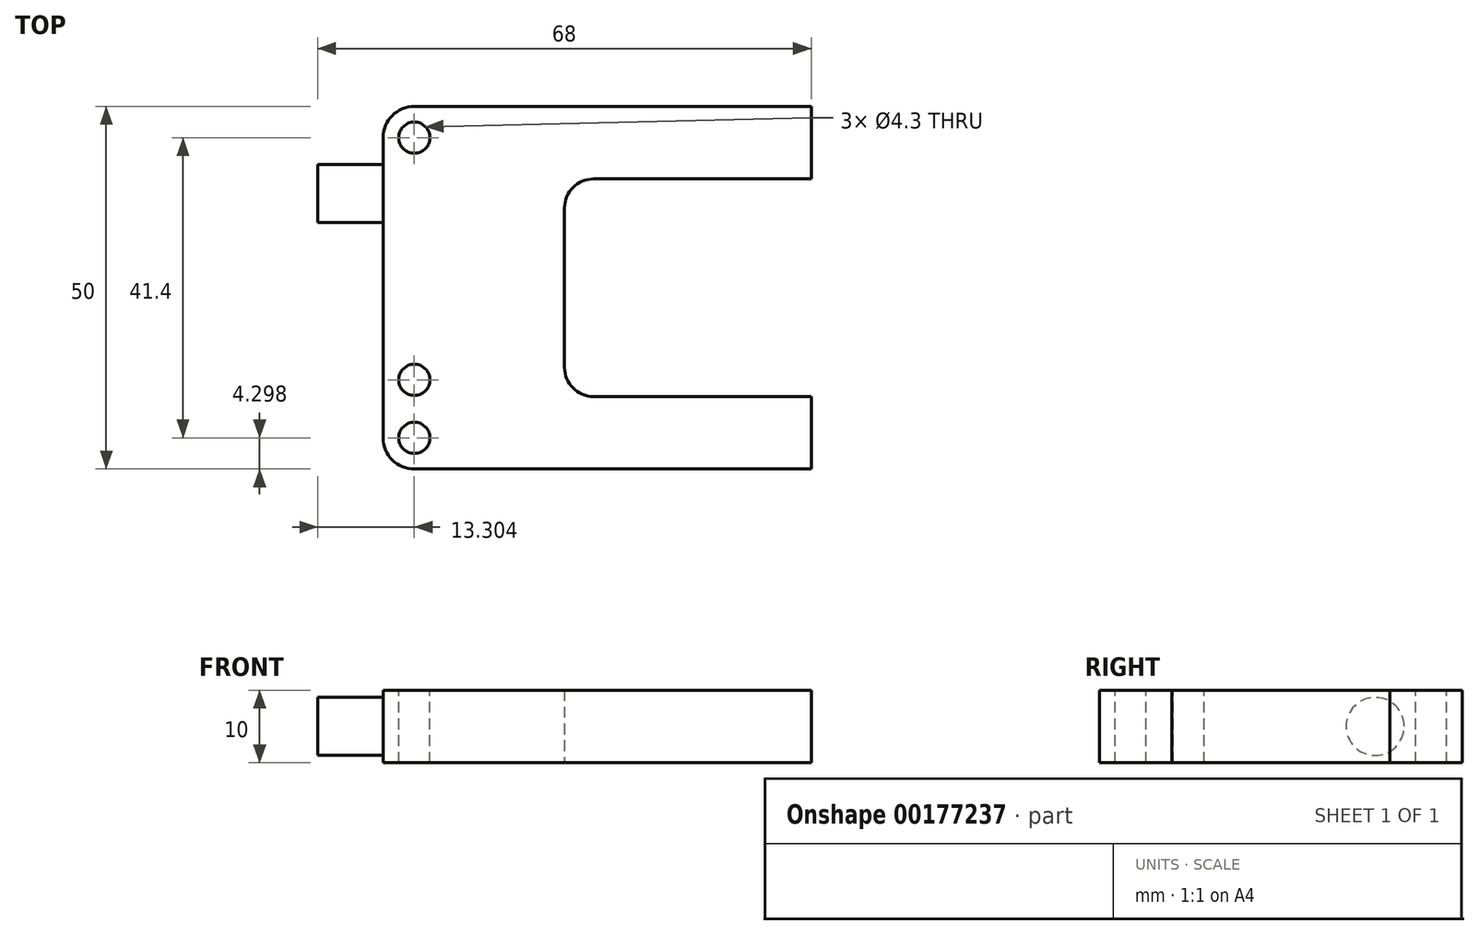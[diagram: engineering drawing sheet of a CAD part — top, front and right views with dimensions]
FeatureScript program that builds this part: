
annotation { "Feature Type Name" : "Feature", "Feature Type Description" : "" }
export const myFeature = defineFeature(function(context is Context, id is Id, definition is map)
    precondition{}
    {
        {
            var Q0;
            Q0=qCreatedBy(makeId("Top.planeOp"),FACE);
            var sketch = newSketch(context, id + "F0", { "sketchPlane" : qUnion([Q0])});
            skLineSegment(sketch, "E0", {"start": v(-16.13, 24.59) * mm, "end": v(42.87, 24.59) * mm});
            skLineSegment(sketch, "E1", {"start": v(42.87, 24.59) * mm, "end": v(42.87, 14.59) * mm});
            skLineSegment(sketch, "E2", {"start": v(42.87, 14.59) * mm, "end": v(8.87, 14.59) * mm});
            skLineSegment(sketch, "E3", {"start": v(8.87, 14.59) * mm, "end": v(8.87, -15.41) * mm});
            skLineSegment(sketch, "E4", {"start": v(8.87, -15.41) * mm, "end": v(42.87, -15.41) * mm});
            skLineSegment(sketch, "E5", {"start": v(42.87, -15.41) * mm, "end": v(42.87, -25.41) * mm});
            skLineSegment(sketch, "E6", {"start": v(42.87, -25.41) * mm, "end": v(-16.13, -25.41) * mm});
            skLineSegment(sketch, "E7", {"start": v(-16.13, -25.41) * mm, "end": v(-16.13, 24.59) * mm});
            skSolve(sketch);
        }
        {
            var Q0;
            Q0 = qSketchRegion(id + "F0", true);
            extrude(context, id + "F1", {"entities" : qUnion([Q0]), "depth" : 10 * mm});
        }
        {
            var Q0;
            Q0=makeQuery(id+"F1.opExtrude","SWEPT_EDGE",EDGE,{"disambiguationData":[OSD([sQuery(id+"F0.wireOp",EDGE,"E2"),sQuery(id+"F0.wireOp",EDGE,"E3")])]});
            var Q1;
            Q1=makeQuery(id+"F1.opExtrude","SWEPT_EDGE",EDGE,{"disambiguationData":[OSD([sQuery(id+"F0.wireOp",EDGE,"E3"),sQuery(id+"F0.wireOp",EDGE,"E4")])]});
            fillet(context, id + "F2", {"entities" : qUnion([Q0, Q1]), "radius" : 4 * mm, "tangentPropagation" : true, "allowEdgeOverflow" : false});
        }
        {
            var Q0;
            Q0=makeQuery(id+"F1.opExtrude","SWEPT_EDGE",EDGE,{"disambiguationData":[OSD([sQuery(id+"F0.wireOp",EDGE,"E0"),sQuery(id+"F0.wireOp",EDGE,"E7")])]});
            var Q1;
            Q1=makeQuery(id+"F1.opExtrude","SWEPT_EDGE",EDGE,{"disambiguationData":[OSD([sQuery(id+"F0.wireOp",EDGE,"E6"),sQuery(id+"F0.wireOp",EDGE,"E7")])]});
            fillet(context, id + "F3", {"entities" : qUnion([Q0, Q1]), "radius" : 4.3 * mm, "tangentPropagation" : true, "allowEdgeOverflow" : false});
        }
        {
            var Q0;
            Q0=makeQuery(id+"F1.opExtrude","CAP_FACE",FACE,{"disambiguationData":[OSD([sQuery(id+"F0.wireOp",EDGE,"E0"),sQuery(id+"F0.wireOp",EDGE,"E1"),sQuery(id+"F0.wireOp",EDGE,"E2"),sQuery(id+"F0.wireOp",EDGE,"E3"),sQuery(id+"F0.wireOp",EDGE,"E4"),sQuery(id+"F0.wireOp",EDGE,"E5"),sQuery(id+"F0.wireOp",EDGE,"E6"),sQuery(id+"F0.wireOp",EDGE,"E7")])],"isStart":false});
            var sketch = newSketch(context, id + "F4", { "sketchPlane" : qUnion([Q0])});
            skPoint(sketch, "E8", {"position": v(-11.83, 20.29) * mm});
            skPoint(sketch, "E9", {"position": v(-11.83, -21.11) * mm});
            skPoint(sketch, "E10", {"position": v(-11.83, -13.11) * mm});
            skSolve(sketch);
        }
        {
            var Q0;
            Q0=sQuery(id+"F4.wireOp",VERTEX,"E8");
            var Q1;
            Q1=sQuery(id+"F4.wireOp",VERTEX,"E10");
            var Q2;
            Q2=sQuery(id+"F4.wireOp",VERTEX,"E9");
            var Q3;
            Q3=makeQuery(id+"F1.opExtrude","SWEPT_BODY",BODY,{"disambiguationData":[OSD([sQuery(id+"F0.wireOp",EDGE,"E0"),sQuery(id+"F0.wireOp",EDGE,"E1"),sQuery(id+"F0.wireOp",EDGE,"E2"),sQuery(id+"F0.wireOp",EDGE,"E3"),sQuery(id+"F0.wireOp",EDGE,"E4"),sQuery(id+"F0.wireOp",EDGE,"E5"),sQuery(id+"F0.wireOp",EDGE,"E6"),sQuery(id+"F0.wireOp",EDGE,"E7")])]});
            hole(context, id + "F5", {"style" : HoleStyle.SIMPLE, "endStyle" : HoleEndStyle.THROUGH, "holeDiameter" : 4.3 * mm, "locations" : qUnion([Q0, Q1, Q2]), "scope" : qUnion([Q3]), "isTappedThrough" : true});
        }
        {
            var Q0;
            Q0=makeQuery(id+"F1.opExtrude","SWEPT_FACE",FACE,{"disambiguationData":[OSD([sQuery(id+"F0.wireOp",EDGE,"E7")])]});
            var sketch = newSketch(context, id + "F6", { "sketchPlane" : qUnion([Q0])});
            skCircle(sketch, "E11", {"center": v(-12.59, 5) * mm, "radius": 4 * mm});
            skSolve(sketch);
        }
        {
            var Q0;
            Q0 = qSketchRegion(id + "F6", true);
            extrude(context, id + "F7", {"entities" : qUnion([Q0]), "operationType" : NewBodyOperationType.ADD, "depth" : 9 * mm});
        }
    });
